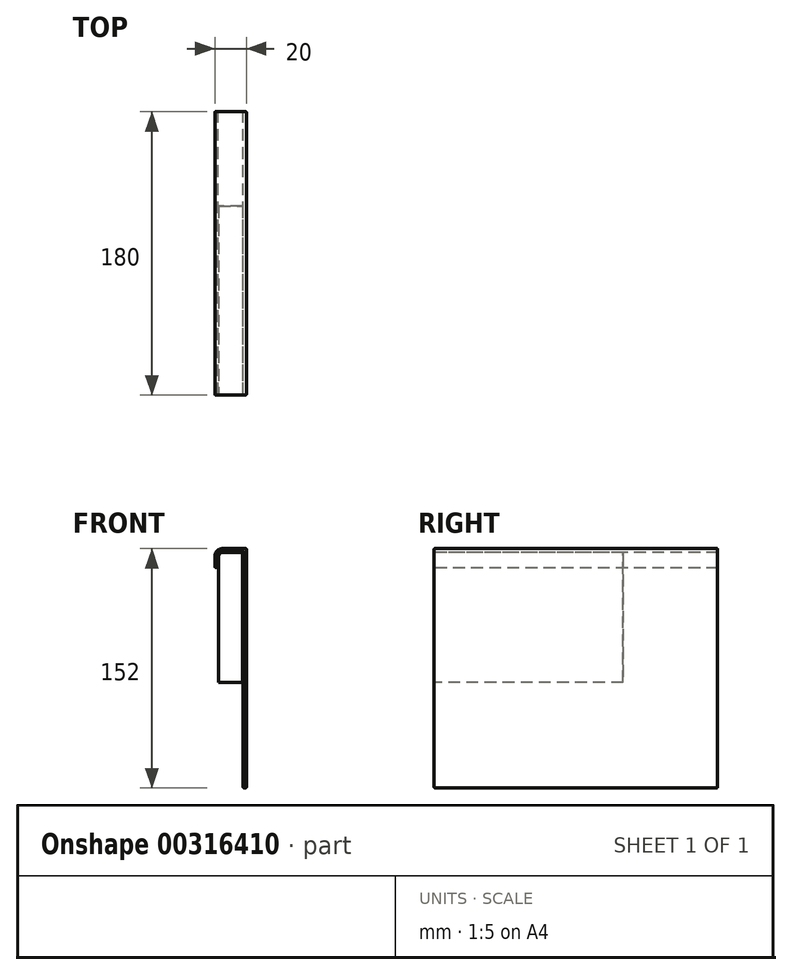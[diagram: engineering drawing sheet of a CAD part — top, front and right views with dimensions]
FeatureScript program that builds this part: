
annotation { "Feature Type Name" : "Feature", "Feature Type Description" : "" }
export const myFeature = defineFeature(function(context is Context, id is Id, definition is map)
    precondition{}
    {
        {
            var Q0;
            Q0=qCreatedBy(makeId("Front.planeOp"),FACE);
            var sketch = newSketch(context, id + "F0", { "sketchPlane" : qUnion([Q0])});
            skLineSegment(sketch, "E0.bottom", {"start": v(0, 0) * mm, "end": v(2, 0) * mm});
            skLineSegment(sketch, "E0.top", {"start": v(0, -150) * mm, "end": v(2, -150) * mm});
            skLineSegment(sketch, "E0.left", {"start": v(0, 0) * mm, "end": v(0, -150) * mm});
            skLineSegment(sketch, "E0.right", {"start": v(2, 0) * mm, "end": v(2, -150) * mm});
            skLineSegment(sketch, "E1.bottom", {"start": v(2, 0) * mm, "end": v(-18, 0) * mm});
            skLineSegment(sketch, "E1.top", {"start": v(2, 2) * mm, "end": v(-18, 2) * mm});
            skLineSegment(sketch, "E1.left", {"start": v(2, 0) * mm, "end": v(2, 2) * mm});
            skLineSegment(sketch, "E1.right", {"start": v(-18, 0) * mm, "end": v(-18, 2) * mm});
            skLineSegment(sketch, "E2.bottom", {"start": v(-18, 0) * mm, "end": v(-16, 0) * mm});
            skLineSegment(sketch, "E2.top", {"start": v(-18, -10) * mm, "end": v(-16, -10) * mm});
            skLineSegment(sketch, "E2.left", {"start": v(-18, 0) * mm, "end": v(-18, -10) * mm});
            skLineSegment(sketch, "E2.right", {"start": v(-16, 0) * mm, "end": v(-16, -10) * mm});
            skSolve(sketch);
        }
        {
            var Q0;
            Q0 = qSketchRegion(id + "F0", true);
            extrude(context, id + "F1", {"entities" : qUnion([Q0]), "depth" : 180 * mm});
        }
        {
            var Q0;
            Q0=makeQuery(id+"F1.opExtrude","SWEPT_EDGE",EDGE,{"disambiguationData":[OSD([sQuery(id+"F0.wireOp",EDGE,"E1.top"),sQuery(id+"F0.wireOp",EDGE,"E1.right")])]});
            fillet(context, id + "F2", {"entities" : qUnion([Q0]), "radius" : 5 * mm, "tangentPropagation" : true, "allowEdgeOverflow" : false});
        }
        {
            var Q0;
            Q0=makeQuery(id+"F1.opExtrude","SWEPT_EDGE",EDGE,{"disambiguationData":[OSD([sQuery(id+"F0.wireOp",EDGE,"E1.bottom"),sQuery(id+"F0.wireOp",EDGE,"E2.bottom"),sQuery(id+"F0.wireOp",EDGE,"E2.right")])]});
            fillet(context, id + "F3", {"entities" : qUnion([Q0]), "radius" : 3 * mm, "tangentPropagation" : true, "allowEdgeOverflow" : false});
        }
        {
            var Q0;
            Q0=makeQuery(id+"F1.opExtrude","CAP_FACE",FACE,{"disambiguationData":[OSD([sQuery(id+"F0.wireOp",EDGE,"E0.top"),sQuery(id+"F0.wireOp",EDGE,"E0.left"),sQuery(id+"F0.wireOp",EDGE,"E0.right"),sQuery(id+"F0.wireOp",EDGE,"E1.bottom"),sQuery(id+"F0.wireOp",EDGE,"E1.top"),sQuery(id+"F0.wireOp",EDGE,"E1.left"),sQuery(id+"F0.wireOp",EDGE,"E1.right"),sQuery(id+"F0.wireOp",EDGE,"E2.top"),sQuery(id+"F0.wireOp",EDGE,"E2.left"),sQuery(id+"F0.wireOp",EDGE,"E2.right")])],"isStart":false});
            var Q1;
            Q1=makeQuery(id+"F1.opExtrude","CAP_FACE",FACE,{"disambiguationData":[OSD([sQuery(id+"F0.wireOp",EDGE,"E0.top"),sQuery(id+"F0.wireOp",EDGE,"E0.left"),sQuery(id+"F0.wireOp",EDGE,"E0.right"),sQuery(id+"F0.wireOp",EDGE,"E1.bottom"),sQuery(id+"F0.wireOp",EDGE,"E1.top"),sQuery(id+"F0.wireOp",EDGE,"E1.left"),sQuery(id+"F0.wireOp",EDGE,"E1.right"),sQuery(id+"F0.wireOp",EDGE,"E2.top"),sQuery(id+"F0.wireOp",EDGE,"E2.left"),sQuery(id+"F0.wireOp",EDGE,"E2.right")])],"isStart":true});
            var Q2;
            Q2=makeQuery(id+"F1.opExtrude","SWEPT_FACE",FACE,{"disambiguationData":[OSD([sQuery(id+"F0.wireOp",EDGE,"E0.top")])]});
            var Q3;
            Q3=makeQuery(id+"F1.opExtrude","SWEPT_FACE",FACE,{"disambiguationData":[OSD([sQuery(id+"F0.wireOp",EDGE,"E2.top")])]});
            fillet(context, id + "F4", {"entities" : qUnion([Q0, Q1, Q2, Q3]), "radius" : 0.5 * mm, "tangentPropagation" : true, "allowEdgeOverflow" : false});
        }
        {
            var Q0;
            Q0=makeQuery(id+"F1.opExtrude","SWEPT_EDGE",EDGE,{"disambiguationData":[OSD([sQuery(id+"F0.wireOp",EDGE,"E0.left"),sQuery(id+"F0.wireOp",EDGE,"E1.bottom")])]});
            var Q1;
            Q1=makeQuery(id+"F1.opExtrude","SWEPT_EDGE",EDGE,{"disambiguationData":[OSD([sQuery(id+"F0.wireOp",EDGE,"E1.top"),sQuery(id+"F0.wireOp",EDGE,"E1.left")])]});
            fillet(context, id + "F5", {"entities" : qUnion([Q0, Q1]), "radius" : 0.5 * mm, "tangentPropagation" : true, "allowEdgeOverflow" : false});
        }
        {
            var Q0;
            Q0=makeQuery(id+"F1.opExtrude","CAP_FACE",FACE,{"disambiguationData":[OSD([sQuery(id+"F0.wireOp",EDGE,"E0.top"),sQuery(id+"F0.wireOp",EDGE,"E0.left"),sQuery(id+"F0.wireOp",EDGE,"E0.right"),sQuery(id+"F0.wireOp",EDGE,"E1.bottom"),sQuery(id+"F0.wireOp",EDGE,"E1.top"),sQuery(id+"F0.wireOp",EDGE,"E1.left"),sQuery(id+"F0.wireOp",EDGE,"E1.right"),sQuery(id+"F0.wireOp",EDGE,"E2.top"),sQuery(id+"F0.wireOp",EDGE,"E2.left"),sQuery(id+"F0.wireOp",EDGE,"E2.right")])],"isStart":false});
            var sketch = newSketch(context, id + "F6", { "sketchPlane" : qUnion([Q0])});
            skLineSegment(sketch, "E3.0", {"start": v(0, -149.5) * mm, "end": v(0, -0.5) * mm});
            skArc(sketch, "E4.0", {"start": v(-0.5, 0) * mm, "mid": v(-0.15, -0.15) * mm, "end": v(0, -0.5) * mm});
            skLineSegment(sketch, "E5.0", {"start": v(-0.5, 0) * mm, "end": v(-13, 0) * mm});
            skArc(sketch, "E6.0", {"start": v(-13, 0) * mm, "mid": v(-15.12, -0.88) * mm, "end": v(-16, -3) * mm});
            skLineSegment(sketch, "E7.0", {"start": v(-16, -3) * mm, "end": v(-16, -9.5) * mm});
            skLineSegment(sketch, "E8.0", {"start": v(-15.5, -3) * mm, "end": v(-15.5, -83) * mm});
            skArc(sketch, "E8.1", {"start": v(-13, -0.5) * mm, "mid": v(-14.77, -1.23) * mm, "end": v(-15.5, -3) * mm});
            skLineSegment(sketch, "E8.2", {"start": v(-0.5, -0.5) * mm, "end": v(-13, -0.5) * mm});
            skLineSegment(sketch, "E8.3", {"start": v(-0.5, -29.5) * mm, "end": v(-0.5, -0.5) * mm});
            skLineSegment(sketch, "E9", {"start": v(-15.5, -83) * mm, "end": v(-0.5, -83) * mm});
            skLineSegment(sketch, "E10", {"start": v(-0.5, -83) * mm, "end": v(-0.5, -29.5) * mm});
            skSolve(sketch);
        }
        {
            var Q0;
            Q0=makeQuery(id+"F6.imprint","IMPRINT",FACE,{"disambiguationData":[TD([[makeQuery(id+"F6.imprint","IMPRINT",EDGE,{"derivedFrom":sQuery(id+"F6.wireOp",EDGE,"E8.0")}),1.0]])]});
            extrude(context, id + "F7", {"entities" : qUnion([Q0]), "oppositeDirection" : true, "depth" : 120 * mm});
        }
    });
